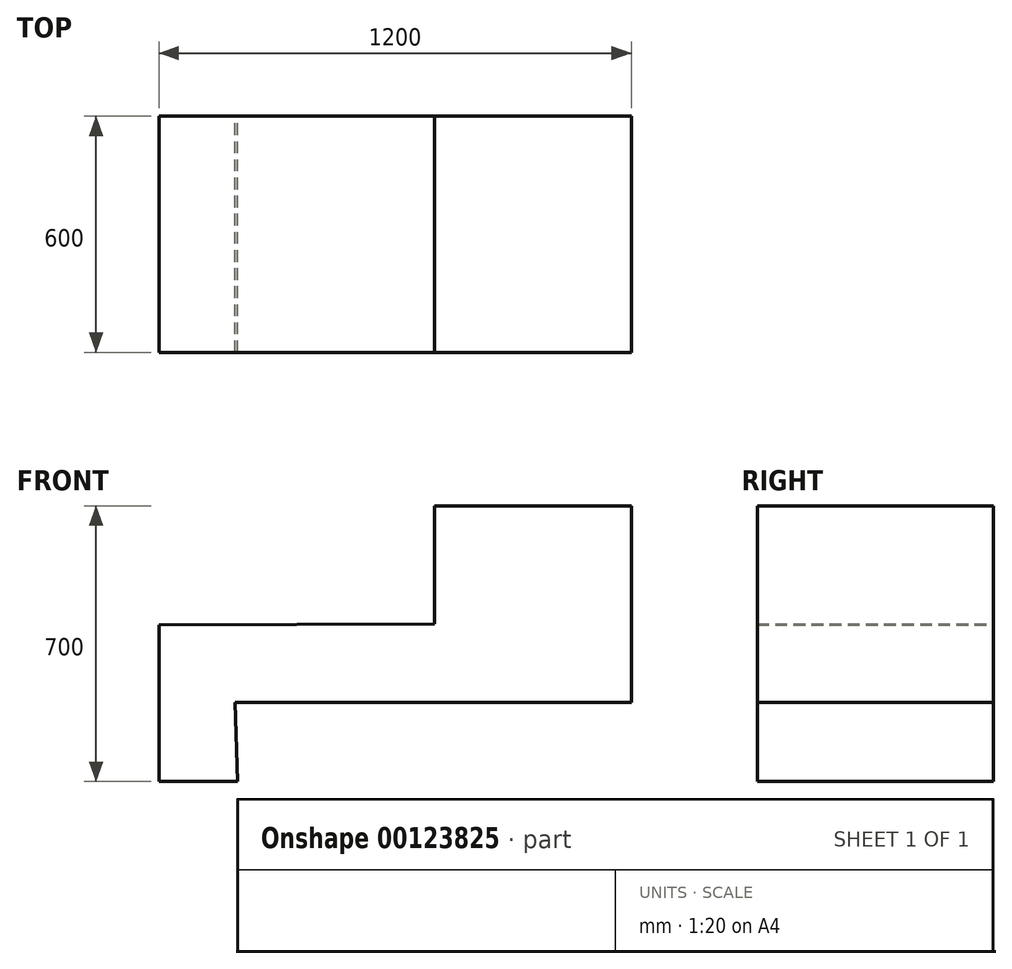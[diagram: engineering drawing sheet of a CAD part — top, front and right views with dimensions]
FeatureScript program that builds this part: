
annotation { "Feature Type Name" : "Feature", "Feature Type Description" : "" }
export const myFeature = defineFeature(function(context is Context, id is Id, definition is map)
    precondition{}
    {
        {
            var Q0;
            Q0=qCreatedBy(makeId("Front.planeOp"),FACE);
            var sketch = newSketch(context, id + "F0", { "sketchPlane" : qUnion([Q0])});
            skLineSegment(sketch, "E0.bottom", {"start": v(100, 350) * mm, "end": v(600, 350) * mm});
            skLineSegment(sketch, "E0.top", {"start": v(-600, -350) * mm, "end": v(-400, -350) * mm});
            skLineSegment(sketch, "E0.left", {"start": v(-600, 47.15) * mm, "end": v(-600, -350) * mm});
            skLineSegment(sketch, "E0.right", {"start": v(600, 350) * mm, "end": v(600, -150) * mm});
            skPoint(sketch, "E0.middle", {"position": v(0, 0) * mm});
            skLineSegment(sketch, "E1", {"start": v(-400, -350) * mm, "end": v(-406.4, -150) * mm});
            skLineSegment(sketch, "E2", {"start": v(-406.4, -150) * mm, "end": v(600, -150) * mm});
            skPoint(sketch, "E3.orphan", {"position": v(600, -350) * mm});
            skLineSegment(sketch, "E4", {"start": v(600, 350) * mm, "end": v(100, 350) * mm});
            skLineSegment(sketch, "E5", {"start": v(100, 350) * mm, "end": v(100, 50) * mm});
            skLineSegment(sketch, "E6", {"start": v(100, 50) * mm, "end": v(-600, 47.15) * mm});
            skPoint(sketch, "E7.orphan", {"position": v(-600, 350) * mm});
            skSolve(sketch);
        }
        {
            var Q0;
            Q0 = qSketchRegion(id + "F0", true);
            extrude(context, id + "F1", {"entities" : qUnion([Q0]), "depth" : 600 * mm});
        }
    });
